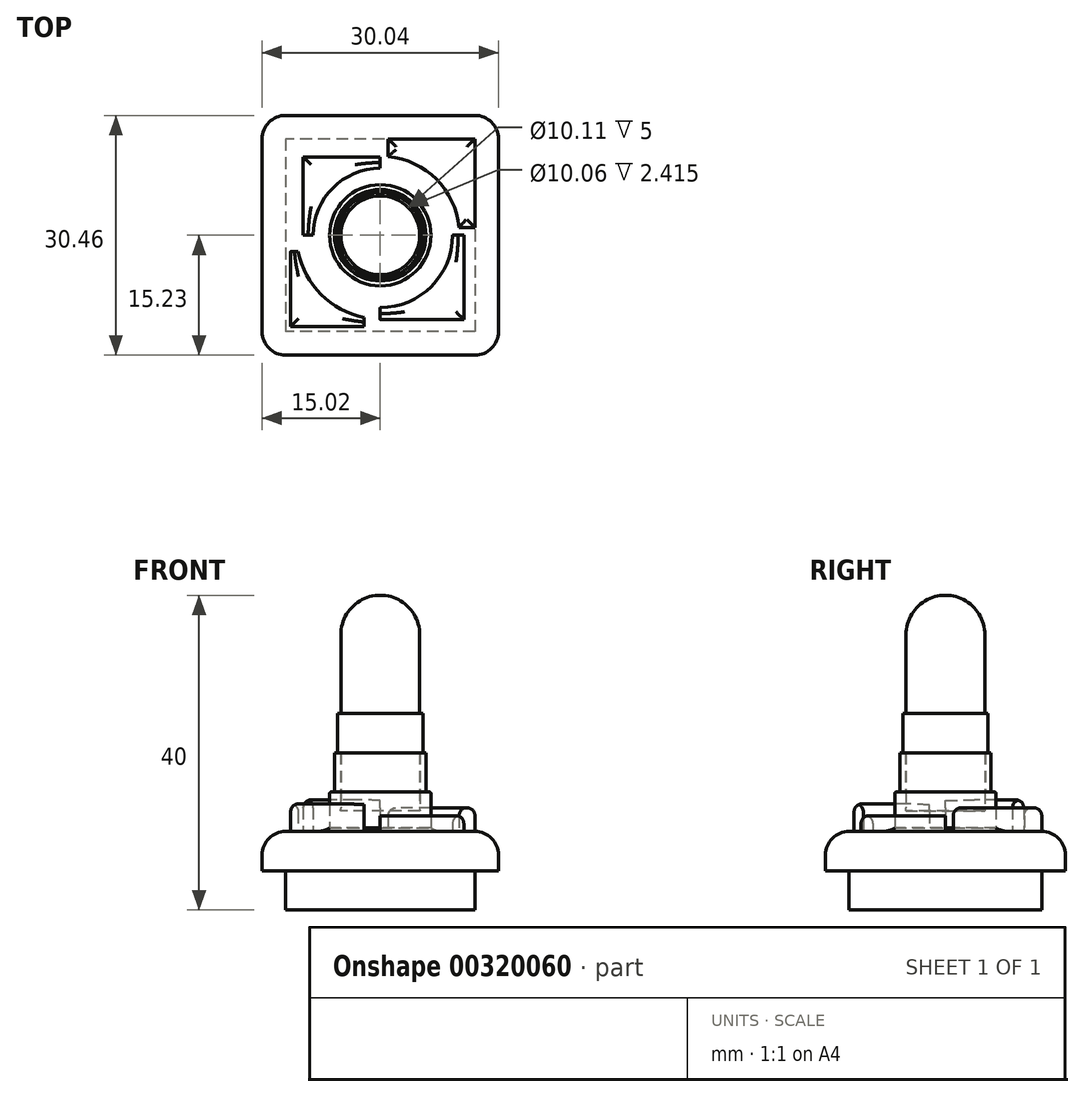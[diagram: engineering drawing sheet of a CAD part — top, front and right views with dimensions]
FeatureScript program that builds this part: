
annotation { "Feature Type Name" : "Feature", "Feature Type Description" : "" }
export const myFeature = defineFeature(function(context is Context, id is Id, definition is map)
    precondition{}
    {
        {
            var Q0;
            Q0=qCreatedBy(makeId("Top.planeOp"),FACE);
            var sketch = newSketch(context, id + "F0", { "sketchPlane" : qUnion([Q0])});
            skLineSegment(sketch, "E0.bottom", {"start": v(12.02, 15.23) * mm, "end": v(-12.02, 15.23) * mm});
            skLineSegment(sketch, "E0.top", {"start": v(12.02, -15.23) * mm, "end": v(-12.02, -15.23) * mm});
            skLineSegment(sketch, "E0.left", {"start": v(15.02, 12.23) * mm, "end": v(15.02, -12.23) * mm});
            skLineSegment(sketch, "E0.right", {"start": v(-15.02, 12.23) * mm, "end": v(-15.02, -12.23) * mm});
            skPoint(sketch, "E0.middle", {"position": v(0, 0) * mm});
            skPoint(sketch, "E1.visualSharp", {"position": v(15.02, 15.23) * mm});
            skArc(sketch, "E1.filletArc", {"start": v(15.02, 12.23) * mm, "mid": v(14.14, 14.35) * mm, "end": v(12.02, 15.23) * mm});
            skPoint(sketch, "E2.visualSharp", {"position": v(-15.02, 15.23) * mm});
            skArc(sketch, "E2.filletArc", {"start": v(-12.02, 15.23) * mm, "mid": v(-14.14, 14.35) * mm, "end": v(-15.02, 12.23) * mm});
            skPoint(sketch, "E3.visualSharp", {"position": v(-15.02, -15.23) * mm});
            skArc(sketch, "E3.filletArc", {"start": v(-15.02, -12.23) * mm, "mid": v(-14.14, -14.35) * mm, "end": v(-12.02, -15.23) * mm});
            skPoint(sketch, "E4.visualSharp", {"position": v(15.02, -15.23) * mm});
            skArc(sketch, "E4.filletArc", {"start": v(12.02, -15.23) * mm, "mid": v(14.14, -14.35) * mm, "end": v(15.02, -12.23) * mm});
            skSolve(sketch);
        }
        {
            var Q0;
            Q0 = qSketchRegion(id + "F0", true);
            extrude(context, id + "F1", {"entities" : qUnion([Q0]), "depth" : 5 * mm});
        }
        {
            var Q0;
            Q0=makeQuery(id+"F1.opExtrude","CAP_FACE",FACE,{"disambiguationData":[OSD([sQuery(id+"F0.wireOp",EDGE,"E0.bottom"),sQuery(id+"F0.wireOp",EDGE,"E0.top"),sQuery(id+"F0.wireOp",EDGE,"E0.left"),sQuery(id+"F0.wireOp",EDGE,"E0.right"),sQuery(id+"F0.wireOp",EDGE,"E1.filletArc"),sQuery(id+"F0.wireOp",EDGE,"E2.filletArc"),sQuery(id+"F0.wireOp",EDGE,"E3.filletArc"),sQuery(id+"F0.wireOp",EDGE,"E4.filletArc")])],"isStart":false});
            var sketch = newSketch(context, id + "F2", { "sketchPlane" : qUnion([Q0])});
            skCircle(sketch, "E5", {"center": v(0, 0) * mm, "radius": 5 * mm});
            skSolve(sketch);
        }
        {
            var Q0;
            Q0 = qSketchRegion(id + "F2", true);
            extrude(context, id + "F3", {"entities" : qUnion([Q0]), "operationType" : NewBodyOperationType.ADD, "depth" : 30 * mm});
        }
        {
            var Q0;
            Q0=makeQuery(id+"F1.opExtrude","CAP_FACE",FACE,{"disambiguationData":[OSD([sQuery(id+"F0.wireOp",EDGE,"E0.bottom"),sQuery(id+"F0.wireOp",EDGE,"E0.top"),sQuery(id+"F0.wireOp",EDGE,"E0.left"),sQuery(id+"F0.wireOp",EDGE,"E0.right"),sQuery(id+"F0.wireOp",EDGE,"E1.filletArc"),sQuery(id+"F0.wireOp",EDGE,"E2.filletArc"),sQuery(id+"F0.wireOp",EDGE,"E3.filletArc"),sQuery(id+"F0.wireOp",EDGE,"E4.filletArc")])],"isStart":false});
            fillet(context, id + "F4", {"entities" : qUnion([Q0]), "radius" : 3 * mm, "tangentPropagation" : true, "allowEdgeOverflow" : false});
        }
        {
            var Q0;
            Q0=makeQuery(id+"F3.opExtrude","CAP_FACE",FACE,{"disambiguationData":[OSD([sQuery(id+"F2.wireOp",EDGE,"E5")])],"isStart":false});
            fillet(context, id + "F5", {"entities" : qUnion([Q0]), "radius" : 5 * mm, "tangentPropagation" : true, "allowEdgeOverflow" : false});
        }
        {
            var Q0;
            Q0=makeQuery(id+"F1.opExtrude","CAP_FACE",FACE,{"disambiguationData":[OSD([sQuery(id+"F0.wireOp",EDGE,"E0.bottom"),sQuery(id+"F0.wireOp",EDGE,"E0.top"),sQuery(id+"F0.wireOp",EDGE,"E0.left"),sQuery(id+"F0.wireOp",EDGE,"E0.right"),sQuery(id+"F0.wireOp",EDGE,"E1.filletArc"),sQuery(id+"F0.wireOp",EDGE,"E2.filletArc"),sQuery(id+"F0.wireOp",EDGE,"E3.filletArc"),sQuery(id+"F0.wireOp",EDGE,"E4.filletArc")])],"isStart":false});
            var sketch = newSketch(context, id + "F6", { "sketchPlane" : qUnion([Q0])});
            skPoint(sketch, "E6.startSnap0", {"position": v(0, 12.23) * mm});
            skLineSegment(sketch, "E7", {"start": v(1, 12.23) * mm, "end": v(12.02, 12.23) * mm});
            skLineSegment(sketch, "E8", {"start": v(12.02, 12.23) * mm, "end": v(12.02, -12.23) * mm});
            skLineSegment(sketch, "E9", {"start": v(12.02, -12.23) * mm, "end": v(-12.02, -12.23) * mm});
            skLineSegment(sketch, "E10", {"start": v(-12.02, -12.23) * mm, "end": v(-12.02, 12.23) * mm});
            skLineSegment(sketch, "E11", {"start": v(1, 10.12) * mm, "end": v(1, 12.23) * mm});
            skPoint(sketch, "E12.start.orphan", {"position": v(0, 10.12) * mm});
            skLineSegment(sketch, "E13", {"start": v(1, 10.12) * mm, "end": v(1, 10.01) * mm});
            skPoint(sketch, "E14.orphan", {"position": v(0, 8) * mm});
            skPoint(sketch, "E6.end.orphan", {"position": v(0, 12.23) * mm});
            skLineSegment(sketch, "E15", {"start": v(12.02, 1) * mm, "end": v(10.01, 1) * mm});
            skPoint(sketch, "E16.orphan", {"position": v(12.02, 0) * mm});
            skPoint(sketch, "E17.end.orphan", {"position": v(10.01, 1) * mm});
            skPoint(sketch, "E18.end.orphan", {"position": v(10.01, 0) * mm});
            skPoint(sketch, "E18.start.orphan", {"position": v(8, 0) * mm});
            skArc(sketch, "E19", {"start": v(10.01, 1) * mm, "mid": v(7.12, 7.11) * mm, "end": v(1, 10.01) * mm});
            skSolve(sketch);
        }
        {
            var Q0;
            Q0 = qSketchRegion(id + "F6", true);
            extrude(context, id + "F7", {"entities" : qUnion([Q0]), "operationType" : NewBodyOperationType.ADD, "depth" : 3 * mm});
        }
        {
            var Q0;
            Q0=makeQuery(id+"F1.opExtrude","CAP_FACE",FACE,{"disambiguationData":[OSD([sQuery(id+"F0.wireOp",EDGE,"E0.bottom"),sQuery(id+"F0.wireOp",EDGE,"E0.top"),sQuery(id+"F0.wireOp",EDGE,"E0.left"),sQuery(id+"F0.wireOp",EDGE,"E0.right"),sQuery(id+"F0.wireOp",EDGE,"E1.filletArc"),sQuery(id+"F0.wireOp",EDGE,"E2.filletArc"),sQuery(id+"F0.wireOp",EDGE,"E3.filletArc"),sQuery(id+"F0.wireOp",EDGE,"E4.filletArc")])],"isStart":false});
            var sketch = newSketch(context, id + "F8", { "sketchPlane" : qUnion([Q0])});
            skLineSegment(sketch, "E20", {"start": v(9.2, 0) * mm, "end": v(10.6, 0) * mm});
            skArc(sketch, "E21", {"start": v(0, -9.2) * mm, "mid": v(6.5, -6.5) * mm, "end": v(9.2, 0) * mm});
            skLineSegment(sketch, "E22", {"start": v(0, -9.2) * mm, "end": v(0, -10.71) * mm});
            skPoint(sketch, "E23.orphan", {"position": v(8, 0) * mm});
            skLineSegment(sketch, "E24", {"start": v(10.6, 0) * mm, "end": v(10.6, -10.71) * mm});
            skPoint(sketch, "E24.endSnap0", {"position": v(0, -10.71) * mm});
            skLineSegment(sketch, "E25", {"start": v(10.6, -10.71) * mm, "end": v(0, -10.71) * mm});
            skPoint(sketch, "E26.orphan", {"position": v(12.02, 0) * mm});
            skPoint(sketch, "E27.orphan", {"position": v(0, -12.23) * mm});
            skSolve(sketch);
        }
        {
            var Q0;
            Q0 = qSketchRegion(id + "F8", true);
            extrude(context, id + "F9", {"entities" : qUnion([Q0]), "operationType" : NewBodyOperationType.ADD, "depth" : 2 * mm});
        }
        {
            var Q0;
            Q0=makeQuery(id+"F1.opExtrude","CAP_FACE",FACE,{"disambiguationData":[OSD([sQuery(id+"F0.wireOp",EDGE,"E0.bottom"),sQuery(id+"F0.wireOp",EDGE,"E0.top"),sQuery(id+"F0.wireOp",EDGE,"E0.left"),sQuery(id+"F0.wireOp",EDGE,"E0.right"),sQuery(id+"F0.wireOp",EDGE,"E1.filletArc"),sQuery(id+"F0.wireOp",EDGE,"E2.filletArc"),sQuery(id+"F0.wireOp",EDGE,"E3.filletArc"),sQuery(id+"F0.wireOp",EDGE,"E4.filletArc")])],"isStart":false});
            var sketch = newSketch(context, id + "F10", { "sketchPlane" : qUnion([Q0])});
            skLineSegment(sketch, "E28", {"start": v(-8.51, 0) * mm, "end": v(-9.78, 0) * mm});
            skLineSegment(sketch, "E29", {"start": v(0, 9.95) * mm, "end": v(0, 8.51) * mm});
            skArc(sketch, "E30", {"start": v(0, 8.51) * mm, "mid": v(-6.02, 6.02) * mm, "end": v(-8.51, 0) * mm});
            skPoint(sketch, "E31.orphan", {"position": v(-12.02, 0) * mm});
            skPoint(sketch, "E32.orphan", {"position": v(-10.01, 0) * mm});
            skPoint(sketch, "E33.orphan", {"position": v(-8, 0) * mm});
            skLineSegment(sketch, "E34", {"start": v(0, 9.95) * mm, "end": v(-9.78, 9.95) * mm});
            skPoint(sketch, "E34.endSnap0", {"position": v(-9.78, 0) * mm});
            skLineSegment(sketch, "E35", {"start": v(-9.78, 9.95) * mm, "end": v(-9.78, 0) * mm});
            skPoint(sketch, "E36.orphan", {"position": v(0, 11.39) * mm});
            skPoint(sketch, "E37.orphan", {"position": v(-11.05, 0) * mm});
            skSolve(sketch);
        }
        {
            var Q0;
            Q0 = qSketchRegion(id + "F10", true);
            extrude(context, id + "F11", {"entities" : qUnion([Q0]), "operationType" : NewBodyOperationType.ADD, "depth" : 4 * mm});
        }
        {
            var Q0;
            Q0=makeQuery(id+"F1.opExtrude","CAP_FACE",FACE,{"disambiguationData":[OSD([sQuery(id+"F0.wireOp",EDGE,"E0.bottom"),sQuery(id+"F0.wireOp",EDGE,"E0.top"),sQuery(id+"F0.wireOp",EDGE,"E0.left"),sQuery(id+"F0.wireOp",EDGE,"E0.right"),sQuery(id+"F0.wireOp",EDGE,"E1.filletArc"),sQuery(id+"F0.wireOp",EDGE,"E2.filletArc"),sQuery(id+"F0.wireOp",EDGE,"E3.filletArc"),sQuery(id+"F0.wireOp",EDGE,"E4.filletArc")])],"isStart":false});
            var sketch = newSketch(context, id + "F12", { "sketchPlane" : qUnion([Q0])});
            skPoint(sketch, "E38.orphan", {"position": v(-12.02, 0) * mm});
            skPoint(sketch, "E39.orphan", {"position": v(0, -12.23) * mm});
            skPoint(sketch, "E40.endSnap0", {"position": v(-9.02, -12.23) * mm});
            skPoint(sketch, "E41.orphan", {"position": v(-12.02, -9.17) * mm});
            skPoint(sketch, "E42.orphan", {"position": v(-12.02, -6.12) * mm});
            skPoint(sketch, "E43.orphan", {"position": v(-12.02, -12.23) * mm});
            skPoint(sketch, "E44.end.orphan", {"position": v(-6.01, -12.23) * mm});
            skLineSegment(sketch, "E45", {"start": v(-11.38, -2.05) * mm, "end": v(-11.38, -11.6) * mm});
            skLineSegment(sketch, "E46", {"start": v(-9.02, -11.6) * mm, "end": v(-11.38, -11.6) * mm});
            skLineSegment(sketch, "E47", {"start": v(-9.02, -11.6) * mm, "end": v(-2.05, -11.6) * mm});
            skArc(sketch, "E48", {"start": v(-10.43, -2.05) * mm, "mid": v(-7.51, -7.52) * mm, "end": v(-2.05, -10.43) * mm});
            skLineSegment(sketch, "E49", {"start": v(-11.38, -2.05) * mm, "end": v(-10.43, -2.05) * mm});
            skLineSegment(sketch, "E50", {"start": v(-2.05, -11.6) * mm, "end": v(-2.05, -10.43) * mm});
            skPoint(sketch, "E51.end.orphan", {"position": v(-2.05, -10.71) * mm});
            skPoint(sketch, "E52.end.orphan", {"position": v(0, -9.95) * mm});
            skPoint(sketch, "E52.start.orphan", {"position": v(0, -11.6) * mm});
            skPoint(sketch, "E53.orphan", {"position": v(-11.38, 0) * mm});
            skPoint(sketch, "E54.orphan", {"position": v(-9.74, 0) * mm});
            skPoint(sketch, "E55.end.orphan", {"position": v(-10.56, -2.05) * mm});
            skPoint(sketch, "E56.end.orphan", {"position": v(-10.56, 0) * mm});
            skSolve(sketch);
        }
        {
            var Q0;
            Q0 = qSketchRegion(id + "F12", true);
            extrude(context, id + "F13", {"entities" : qUnion([Q0]), "operationType" : NewBodyOperationType.ADD, "depth" : 3.5 * mm});
        }
        {
            var Q0;
            Q0=qCreatedBy(makeId("Top.planeOp"),FACE);
            var sketch = newSketch(context, id + "F14", { "sketchPlane" : qUnion([Q0])});
            skCircle(sketch, "E57", {"center": v(0, 0) * mm, "radius": 5.03 * mm});
            skCircle(sketch, "E58", {"center": v(0, 0) * mm, "radius": 6.43 * mm});
            skSolve(sketch);
        }
        {
            var Q0;
            Q0 = qSketchRegion(id + "F14", true);
            extrude(context, id + "F15", {"entities" : qUnion([Q0]), "operationType" : NewBodyOperationType.ADD, "depth" : 10 * mm});
        }
        {
            var Q0;
            Q0=makeQuery(id+"F15.opExtrude","CAP_FACE",FACE,{"disambiguationData":[OSD([sQuery(id+"F14.wireOp",EDGE,"E57"),sQuery(id+"F14.wireOp",EDGE,"E58")])],"isStart":false});
            var sketch = newSketch(context, id + "F16", { "sketchPlane" : qUnion([Q0])});
            skCircle(sketch, "E59", {"center": v(0, 0) * mm, "radius": 5.05 * mm});
            skCircle(sketch, "E60", {"center": v(0, 0) * mm, "radius": 5.8 * mm});
            skSolve(sketch);
        }
        {
            var Q0;
            Q0 = qSketchRegion(id + "F16", true);
            extrude(context, id + "F17", {"entities" : qUnion([Q0]), "operationType" : NewBodyOperationType.ADD, "depth" : 5 * mm});
        }
        {
            var Q0;
            Q0=makeQuery(id+"F17.opExtrude","CAP_FACE",FACE,{"disambiguationData":[OSD([sQuery(id+"F16.wireOp",EDGE,"E59"),sQuery(id+"F16.wireOp",EDGE,"E60")])],"isStart":false});
            var sketch = newSketch(context, id + "F18", { "sketchPlane" : qUnion([Q0])});
            skCircle(sketch, "E61", {"center": v(0, 0) * mm, "radius": 5.43 * mm});
            skSolve(sketch);
        }
        {
            var Q0;
            Q0 = qSketchRegion(id + "F18", true);
            extrude(context, id + "F19", {"entities" : qUnion([Q0]), "operationType" : NewBodyOperationType.ADD, "depth" : 5 * mm});
        }
        {
            var Q0;
            Q0=makeQuery(id+"F13.opExtrude","CAP_FACE",FACE,{"disambiguationData":[OSD([sQuery(id+"F12.wireOp",EDGE,"E45"),sQuery(id+"F12.wireOp",EDGE,"E46"),sQuery(id+"F12.wireOp",EDGE,"E47"),sQuery(id+"F12.wireOp",EDGE,"E48"),sQuery(id+"F12.wireOp",EDGE,"E49"),sQuery(id+"F12.wireOp",EDGE,"E50")])],"isStart":false});
            fillet(context, id + "F20", {"entities" : qUnion([Q0]), "radius" : 1 * mm, "tangentPropagation" : true, "allowEdgeOverflow" : false});
        }
        {
            var Q0;
            Q0=makeQuery(id+"F11.opExtrude","CAP_FACE",FACE,{"disambiguationData":[OSD([sQuery(id+"F10.wireOp",EDGE,"E28"),sQuery(id+"F10.wireOp",EDGE,"E29"),sQuery(id+"F10.wireOp",EDGE,"E30"),sQuery(id+"F10.wireOp",EDGE,"E34"),sQuery(id+"F10.wireOp",EDGE,"E35")])],"isStart":false});
            fillet(context, id + "F21", {"entities" : qUnion([Q0]), "radius" : 1 * mm, "tangentPropagation" : true, "allowEdgeOverflow" : false});
        }
        {
            var Q0;
            Q0=makeQuery(id+"F7.opExtrude","CAP_FACE",FACE,{"disambiguationData":[OSD([sQuery(id+"F6.wireOp",EDGE,"E7"),sQuery(id+"F6.wireOp",EDGE,"E8"),sQuery(id+"F6.wireOp",EDGE,"E11"),sQuery(id+"F6.wireOp",EDGE,"E13"),sQuery(id+"F6.wireOp",EDGE,"E15"),sQuery(id+"F6.wireOp",EDGE,"E19")])],"isStart":false});
            fillet(context, id + "F22", {"entities" : qUnion([Q0]), "radius" : 1 * mm, "tangentPropagation" : true, "allowEdgeOverflow" : false});
        }
        {
            var Q0;
            Q0=makeQuery(id+"F9.opExtrude","CAP_FACE",FACE,{"disambiguationData":[OSD([sQuery(id+"F8.wireOp",EDGE,"E20"),sQuery(id+"F8.wireOp",EDGE,"E21"),sQuery(id+"F8.wireOp",EDGE,"E22"),sQuery(id+"F8.wireOp",EDGE,"E24"),sQuery(id+"F8.wireOp",EDGE,"E25")])],"isStart":false});
            fillet(context, id + "F23", {"entities" : qUnion([Q0]), "radius" : 1 * mm, "tangentPropagation" : true, "allowEdgeOverflow" : false});
        }
        {
            var Q0;
            {var subQ0=sQuery(id+"F14.wireOp",EDGE,"E58");Q0=makeQuery(id+"F17.boolean.opBoolean","SPLIT",FACE,{"disambiguationData":[TD([makeQuery(id+"F15.opExtrude","SWEPT_FACE",FACE,{"disambiguationData":[OSD([subQ0])]})])],"derivedFrom":makeQuery(id+"F15.opExtrude","CAP_FACE",FACE,{"disambiguationData":[OSD([sQuery(id+"F14.wireOp",EDGE,"E57"),subQ0])],"isStart":false})});}
            fillet(context, id + "F24", {"entities" : qUnion([Q0]), "radius" : 0.2 * mm, "tangentPropagation" : true, "allowEdgeOverflow" : false});
        }
        {
            var Q0;
            Q0=makeQuery(id+"F1.opExtrude","CAP_FACE",FACE,{"disambiguationData":[OSD([sQuery(id+"F0.wireOp",EDGE,"E0.bottom"),sQuery(id+"F0.wireOp",EDGE,"E0.top"),sQuery(id+"F0.wireOp",EDGE,"E0.left"),sQuery(id+"F0.wireOp",EDGE,"E0.right"),sQuery(id+"F0.wireOp",EDGE,"E1.filletArc"),sQuery(id+"F0.wireOp",EDGE,"E2.filletArc"),sQuery(id+"F0.wireOp",EDGE,"E3.filletArc"),sQuery(id+"F0.wireOp",EDGE,"E4.filletArc")])],"isStart":true});
            var sketch = newSketch(context, id + "F25", { "sketchPlane" : qUnion([Q0])});
            skLineSegment(sketch, "E62.bottom", {"start": v(12.02, -12.23) * mm, "end": v(-12.02, -12.23) * mm});
            skLineSegment(sketch, "E62.top", {"start": v(12.02, 12.23) * mm, "end": v(-12.02, 12.23) * mm});
            skLineSegment(sketch, "E62.left", {"start": v(12.02, -12.23) * mm, "end": v(12.02, 12.23) * mm});
            skLineSegment(sketch, "E62.right", {"start": v(-12.02, -12.23) * mm, "end": v(-12.02, 12.23) * mm});
            skPoint(sketch, "E62.middle", {"position": v(0, 0) * mm});
            skSolve(sketch);
        }
        {
            var Q0;
            Q0 = qSketchRegion(id + "F25", true);
            extrude(context, id + "F26", {"entities" : qUnion([Q0]), "operationType" : NewBodyOperationType.ADD, "depth" : 5 * mm});
        }
    });
